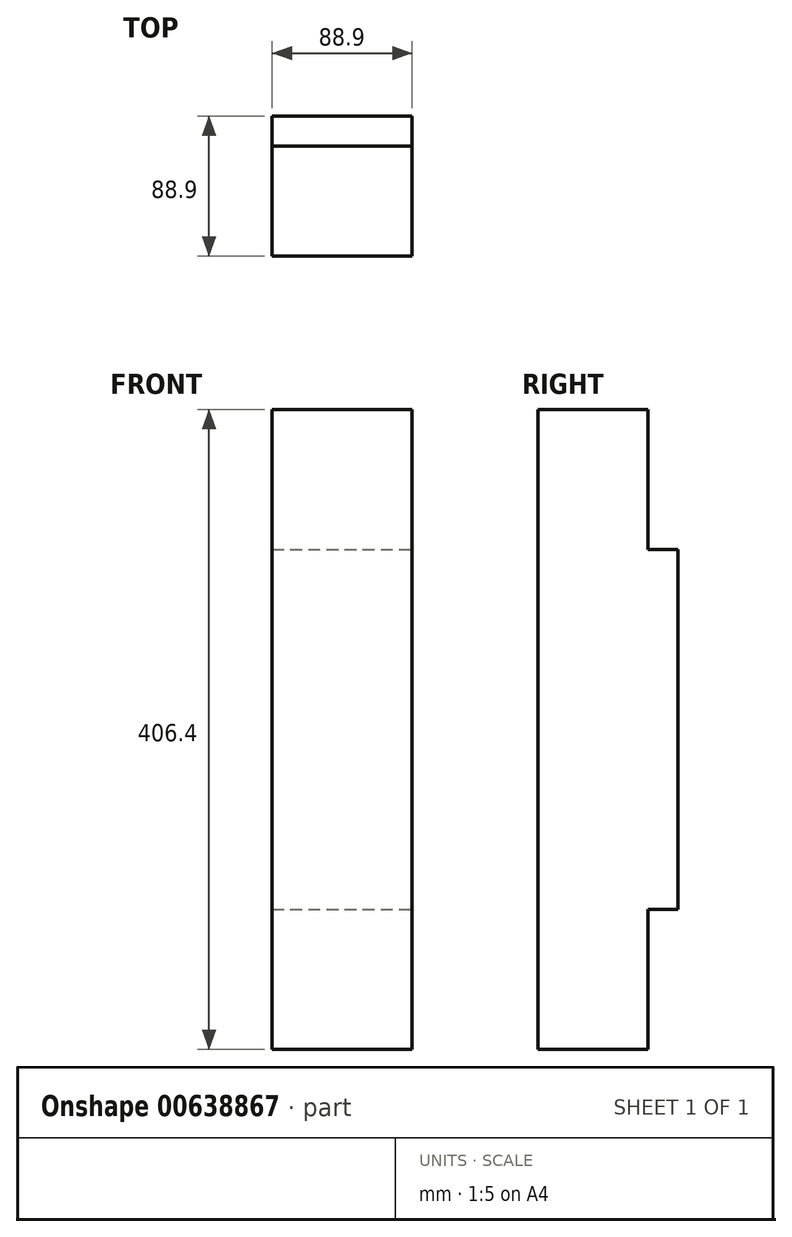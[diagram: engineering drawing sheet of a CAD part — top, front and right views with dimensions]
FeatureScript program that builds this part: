
annotation { "Feature Type Name" : "Feature", "Feature Type Description" : "" }
export const myFeature = defineFeature(function(context is Context, id is Id, definition is map)
    precondition{}
    {
        {
            var Q0;
            Q0=qCreatedBy(makeId("Top.planeOp"),FACE);
            var sketch = newSketch(context, id + "F0", { "sketchPlane" : qUnion([Q0])});
            skLineSegment(sketch, "E0.bottom", {"start": v(44.45, 44.45) * mm, "end": v(-44.45, 44.45) * mm});
            skLineSegment(sketch, "E0.top", {"start": v(44.45, -44.45) * mm, "end": v(-44.45, -44.45) * mm});
            skLineSegment(sketch, "E0.left", {"start": v(44.45, 44.45) * mm, "end": v(44.45, -44.45) * mm});
            skLineSegment(sketch, "E0.right", {"start": v(-44.45, 44.45) * mm, "end": v(-44.45, -44.45) * mm});
            skPoint(sketch, "E0.middle", {"position": v(0, 0) * mm});
            skSolve(sketch);
        }
        {
            var Q0;
            Q0=makeQuery(id+"F0.imprint","IMPRINT",FACE,{"disambiguationData":[TD([[makeQuery(id+"F0.imprint","IMPRINT",EDGE,{"derivedFrom":sQuery(id+"F0.wireOp",EDGE,"E0.bottom")}),1.0]])]});
            extrude(context, id + "F1", {"entities" : qUnion([Q0]), "depth" : 406.4 * mm, "offsetDistance" : 25.4 * mm});
        }
        {
            var Q0;
            Q0=makeQuery(id+"F1.opExtrude","SWEPT_FACE",FACE,{"disambiguationData":[OSD([sQuery(id+"F0.wireOp",EDGE,"E0.left")])]});
            var sketch = newSketch(context, id + "F2", { "sketchPlane" : qUnion([Q0])});
            skLineSegment(sketch, "E1.bottom", {"start": v(44.45, 406.4) * mm, "end": v(25.4, 406.4) * mm});
            skLineSegment(sketch, "E1.top", {"start": v(44.45, 317.5) * mm, "end": v(25.4, 317.5) * mm});
            skLineSegment(sketch, "E1.left", {"start": v(44.45, 406.4) * mm, "end": v(44.45, 317.5) * mm});
            skLineSegment(sketch, "E1.right", {"start": v(25.4, 406.4) * mm, "end": v(25.4, 317.5) * mm});
            skLineSegment(sketch, "E2.bottom", {"start": v(44.45, 0) * mm, "end": v(25.4, 0) * mm});
            skLineSegment(sketch, "E2.top", {"start": v(44.45, 88.9) * mm, "end": v(25.4, 88.9) * mm});
            skLineSegment(sketch, "E2.left", {"start": v(44.45, 0) * mm, "end": v(44.45, 88.9) * mm});
            skLineSegment(sketch, "E2.right", {"start": v(25.4, 0) * mm, "end": v(25.4, 88.9) * mm});
            skSolve(sketch);
        }
        {
            var Q0;
            Q0=makeQuery(id+"F2.imprint","IMPRINT",FACE,{"disambiguationData":[TD([[makeQuery(id+"F2.imprint","IMPRINT",EDGE,{"derivedFrom":sQuery(id+"F2.wireOp",EDGE,"E1.bottom")}),1.0]])]});
            var Q1;
            Q1=makeQuery(id+"F2.imprint","IMPRINT",FACE,{"disambiguationData":[TD([[makeQuery(id+"F2.imprint","IMPRINT",EDGE,{"derivedFrom":sQuery(id+"F2.wireOp",EDGE,"E2.bottom")}),-1.0]])]});
            extrude(context, id + "F3", {"entities" : qUnion([Q0, Q1]), "operationType" : NewBodyOperationType.REMOVE, "endBound" : BoundingType.UP_TO_NEXT, "oppositeDirection" : true, "depth" : 25.4 * mm, "offsetDistance" : 25.4 * mm});
        }
    });
